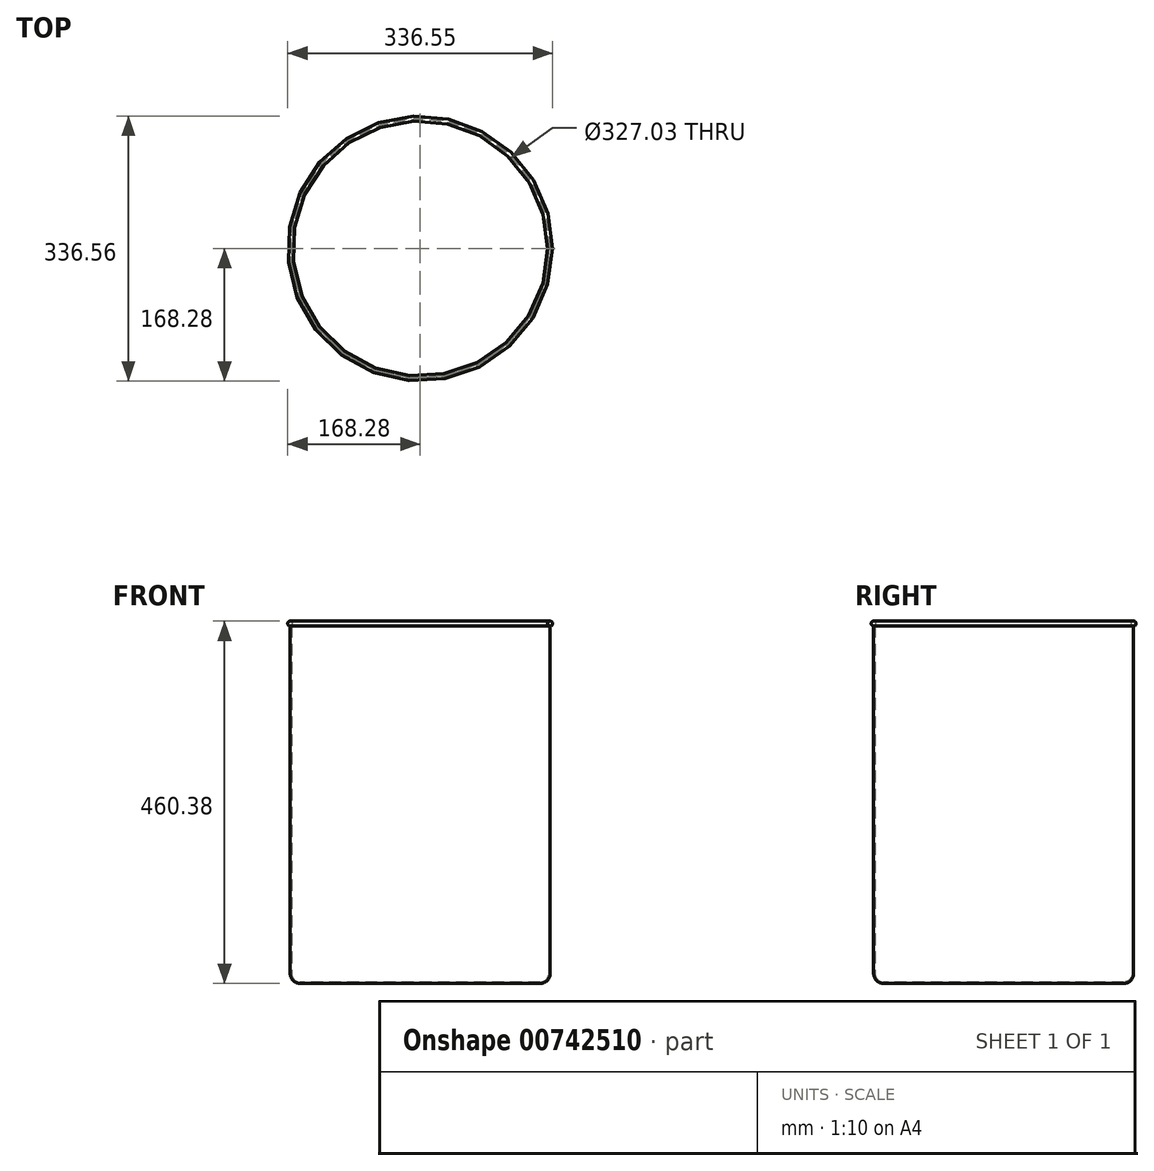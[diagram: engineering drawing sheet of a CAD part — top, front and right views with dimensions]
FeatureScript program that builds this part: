
annotation { "Feature Type Name" : "Feature", "Feature Type Description" : "" }
export const myFeature = defineFeature(function(context is Context, id is Id, definition is map)
    precondition{}
    {
        {
            var Q0;
            Q0=qCreatedBy(makeId("Top.planeOp"),FACE);
            var sketch = newSketch(context, id + "F0", { "sketchPlane" : qUnion([Q0])});
            skCircle(sketch, "E0", {"center": v(0, 0) * mm, "radius": 165.1 * mm});
            skSolve(sketch);
        }
        {
            var Q0;
            Q0 = qSketchRegion(id + "F0", true);
            extrude(context, id + "F1", {"entities" : qUnion([Q0]), "depth" : 457.2 * mm, "offsetDistance" : 25.4 * mm});
        }
        {
            var Q0;
            Q0=makeQuery(id+"F1.opExtrude","CAP_EDGE",EDGE,{"disambiguationData":[OSD([sQuery(id+"F0.wireOp",EDGE,"E0")])],"isStart":true});
            fillet(context, id + "F2", {"entities" : qUnion([Q0]), "radius" : 12.7 * mm, "tangentPropagation" : true, "allowEdgeOverflow" : false});
        }
        {
            var Q0;
            Q0=makeQuery(id+"F1.opExtrude","CAP_FACE",FACE,{"disambiguationData":[OSD([sQuery(id+"F0.wireOp",EDGE,"E0")])],"isStart":false});
            shell(context, id + "F3", {"entities" : qUnion([Q0]), "thickness" : 1.59 * mm});
        }
        {
            var Q0;
            Q0=qCreatedBy(makeId("Front.planeOp"),FACE);
            var sketch = newSketch(context, id + "F4", { "sketchPlane" : qUnion([Q0])});
            skLineSegment(sketch, "E1.0", {"start": v(-165.1, 457.2) * mm, "end": v(165.1, 457.2) * mm});
            skCircle(sketch, "E2", {"center": v(-165.1, 457.2) * mm, "radius": 3.18 * mm});
            skSolve(sketch);
        }
        {
            var Q0;
            Q0 = qSketchRegion(id + "F4", true);
            var Q1;
            Q1=makeQuery(id+"F1.opExtrude","CAP_EDGE",EDGE,{"disambiguationData":[OSD([sQuery(id+"F0.wireOp",EDGE,"E0")])],"isStart":false});
            revolve(context, id + "F5", {"operationType" : NewBodyOperationType.ADD, "surfaceOperationType" : NewSurfaceOperationType.NEW, "entities" : qUnion([Q0]), "axis" : qUnion([Q1]), "revolveType" : RevolveType.FULL});
        }
    });
